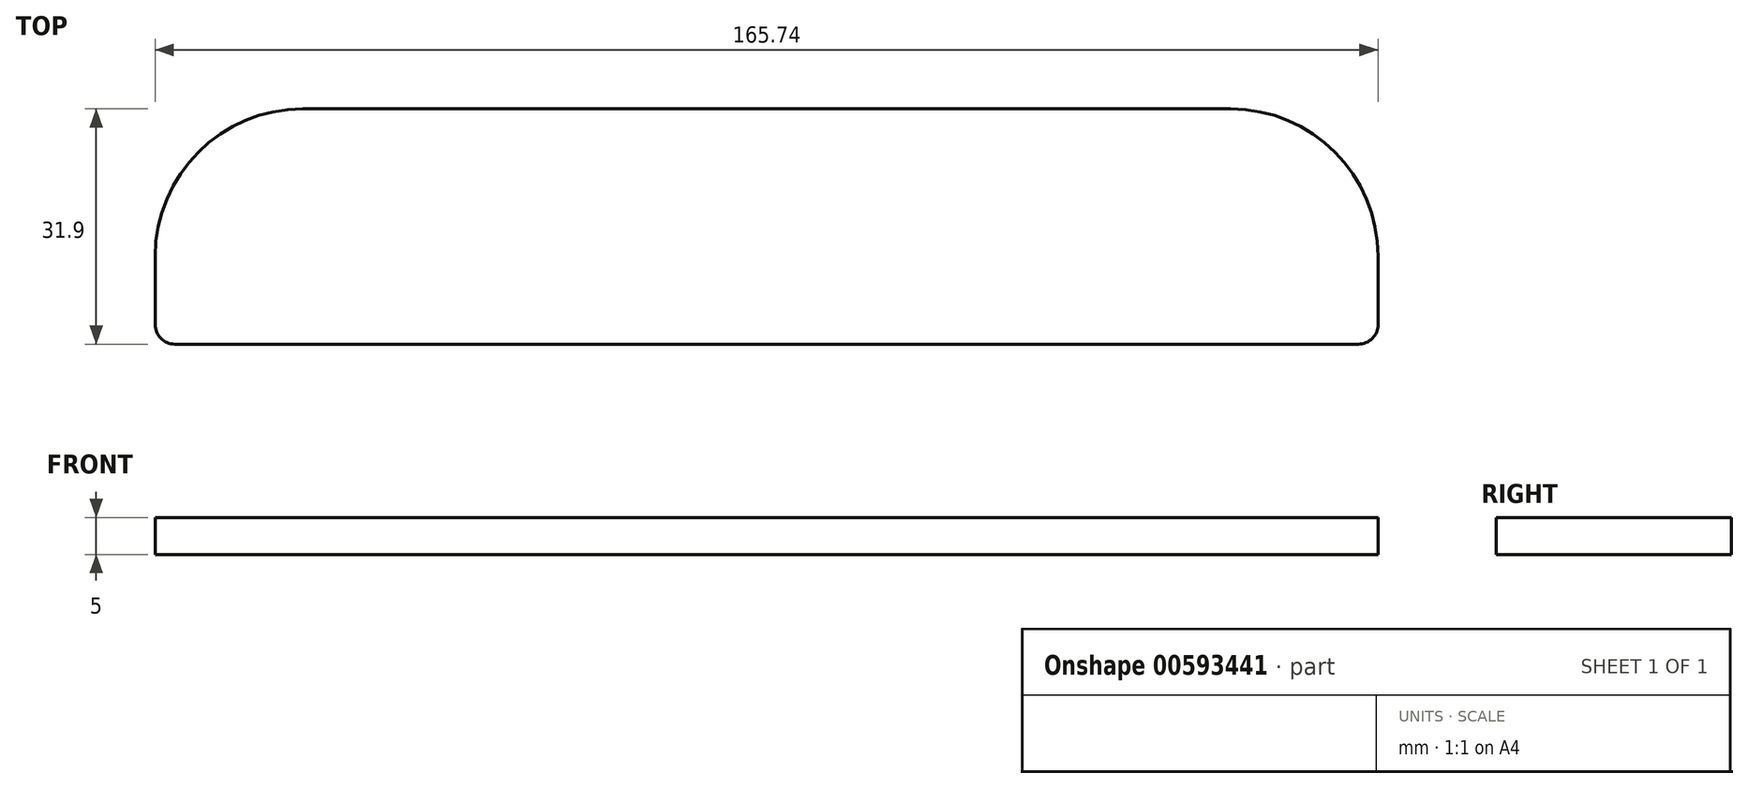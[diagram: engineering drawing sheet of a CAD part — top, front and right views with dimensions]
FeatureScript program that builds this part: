
annotation { "Feature Type Name" : "Feature", "Feature Type Description" : "" }
export const myFeature = defineFeature(function(context is Context, id is Id, definition is map)
    precondition{}
    {
        {
            var Q0;
            Q0=qCreatedBy(makeId("Top.planeOp"),FACE);
            var sketch = newSketch(context, id + "F0", { "sketchPlane" : qUnion([Q0])});
            skLineSegment(sketch, "E0.bottom", {"start": v(82.87, -15.95) * mm, "end": v(-82.87, -15.95) * mm});
            skLineSegment(sketch, "E0.top", {"start": v(62.87, 15.95) * mm, "end": v(-62.87, 15.95) * mm});
            skLineSegment(sketch, "E0.left", {"start": v(82.87, -15.95) * mm, "end": v(82.87, -4.05) * mm});
            skLineSegment(sketch, "E0.right", {"start": v(-82.87, -15.95) * mm, "end": v(-82.87, -4.05) * mm});
            skPoint(sketch, "E0.middle", {"position": v(0, 0) * mm});
            skPoint(sketch, "E1.visualSharp", {"position": v(-82.87, 15.95) * mm});
            skArc(sketch, "E1.filletArc", {"start": v(-62.87, 15.95) * mm, "mid": v(-77, 10.09) * mm, "end": v(-82.87, -4.05) * mm});
            skPoint(sketch, "E2.visualSharp", {"position": v(82.87, 15.95) * mm});
            skArc(sketch, "E2.filletArc", {"start": v(82.87, -4.05) * mm, "mid": v(77, 10.09) * mm, "end": v(62.87, 15.95) * mm});
            skSolve(sketch);
        }
        {
            var Q0;
            Q0=makeQuery(id+"F0.imprint","IMPRINT",FACE,{"disambiguationData":[TD([[makeQuery(id+"F0.imprint","IMPRINT",EDGE,{"derivedFrom":sQuery(id+"F0.wireOp",EDGE,"E0.bottom")}),-1.0]])]});
            extrude(context, id + "F1", {"entities" : qUnion([Q0]), "depth" : 5 * mm, "offsetDistance" : 25 * mm});
        }
        {
            var Q0;
            Q0=makeQuery(id+"F1.opExtrude","SWEPT_EDGE",EDGE,{"disambiguationData":[OSD([sQuery(id+"F0.wireOp",EDGE,"E0.bottom"),sQuery(id+"F0.wireOp",EDGE,"E0.right")])]});
            fillet(context, id + "F2", {"entities" : qUnion([Q0]), "radius" : 2.66 * mm, "tangentPropagation" : true, "allowEdgeOverflow" : false});
        }
        {
            var Q0;
            Q0=makeQuery(id+"F1.opExtrude","SWEPT_EDGE",EDGE,{"disambiguationData":[OSD([sQuery(id+"F0.wireOp",EDGE,"E0.bottom"),sQuery(id+"F0.wireOp",EDGE,"E0.left")])]});
            fillet(context, id + "F3", {"entities" : qUnion([Q0]), "radius" : 2.66 * mm, "tangentPropagation" : true, "allowEdgeOverflow" : false});
        }
    });
